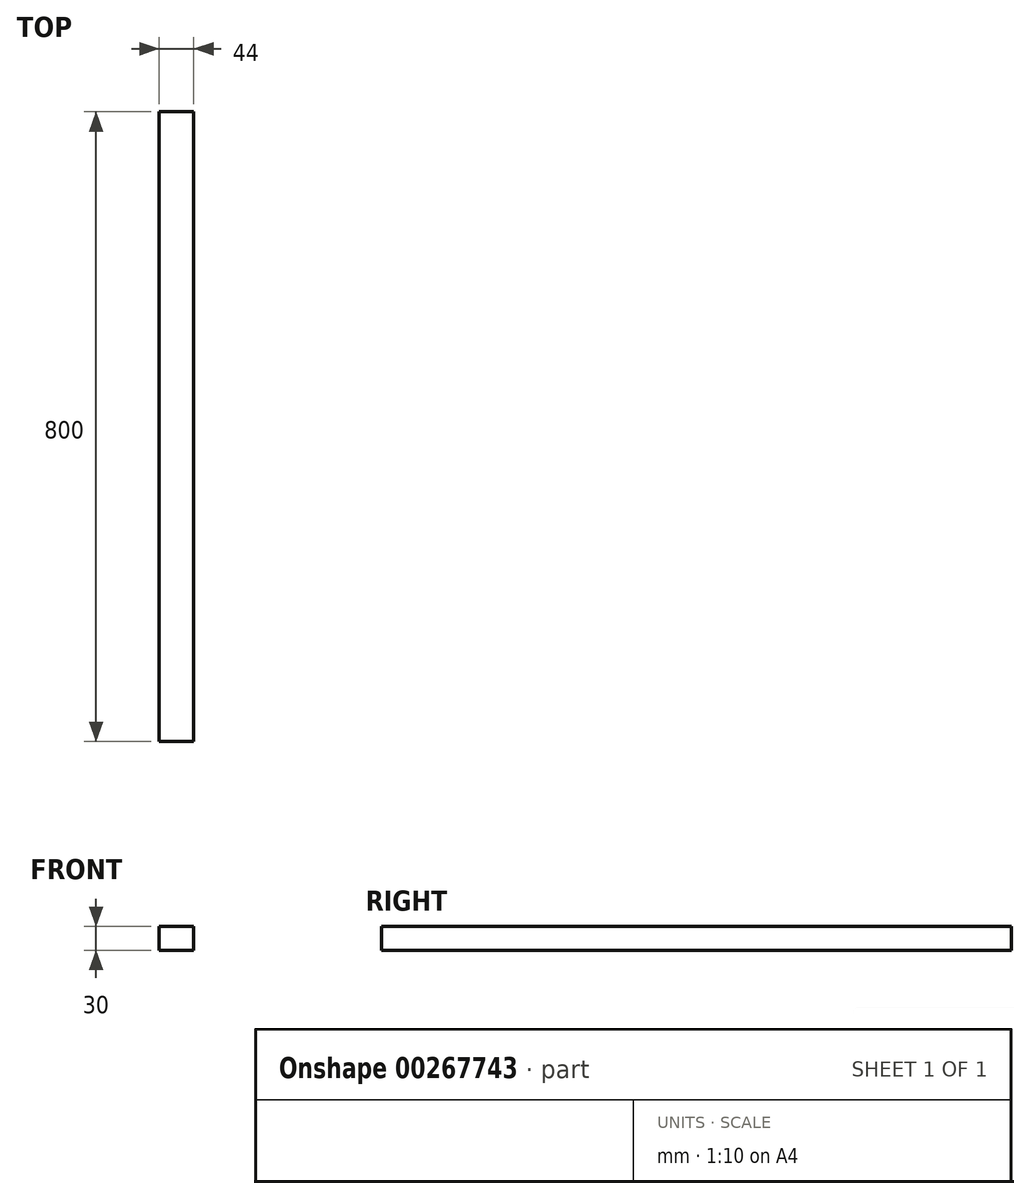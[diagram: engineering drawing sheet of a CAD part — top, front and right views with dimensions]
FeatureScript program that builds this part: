
annotation { "Feature Type Name" : "Feature", "Feature Type Description" : "" }
export const myFeature = defineFeature(function(context is Context, id is Id, definition is map)
    precondition{}
    {
        {
            var Q0;
            Q0=qCreatedBy(makeId("Front.planeOp"),FACE);
            var sketch = newSketch(context, id + "F0", { "sketchPlane" : qUnion([Q0])});
            skLineSegment(sketch, "E0.bottom", {"start": v(22, -15) * mm, "end": v(-22, -15) * mm});
            skLineSegment(sketch, "E0.top", {"start": v(22, 15) * mm, "end": v(-22, 15) * mm});
            skLineSegment(sketch, "E0.left", {"start": v(22, -15) * mm, "end": v(22, 15) * mm});
            skLineSegment(sketch, "E0.right", {"start": v(-22, -15) * mm, "end": v(-22, 15) * mm});
            skPoint(sketch, "E0.middle", {"position": v(0, 0) * mm});
            skSolve(sketch);
        }
        {
            var Q0;
            Q0=qSketchRegion(id+"F0",true);
            extrude(context, id + "F1", {"entities" : qUnion([Q0]), "oppositeDirection" : true, "depth" : 800 * mm});
        }
    });
